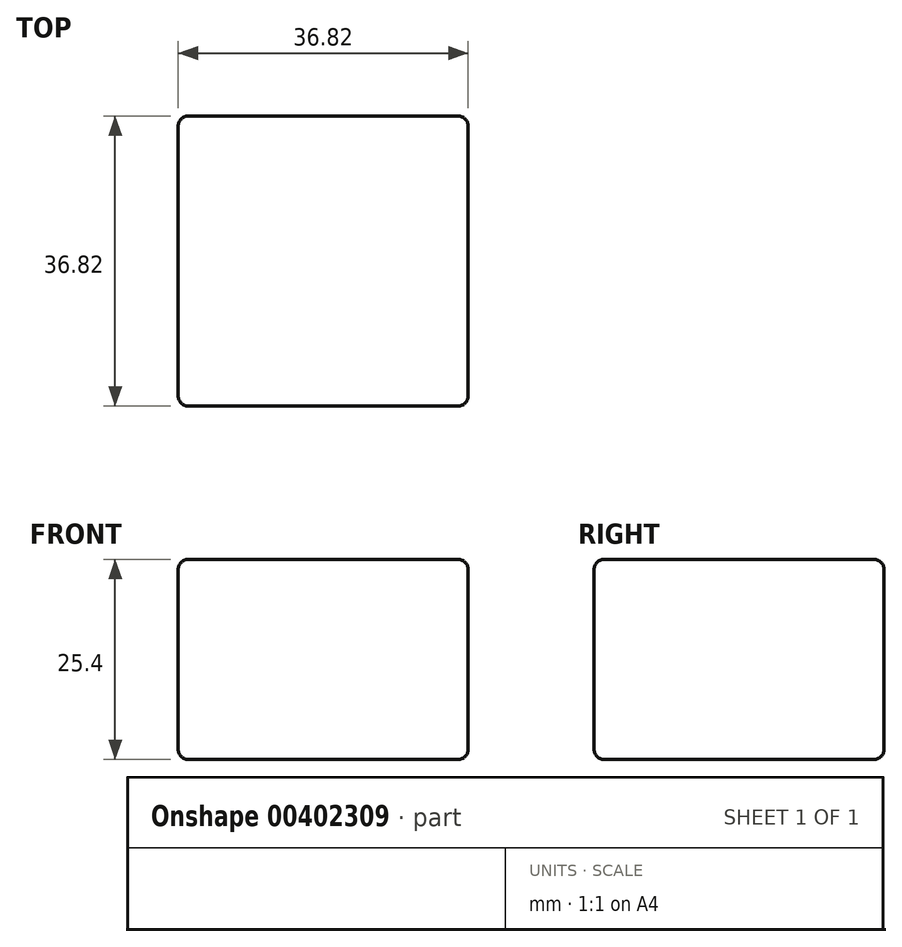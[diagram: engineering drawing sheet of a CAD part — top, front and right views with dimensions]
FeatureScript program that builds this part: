
annotation { "Feature Type Name" : "Feature", "Feature Type Description" : "" }
export const myFeature = defineFeature(function(context is Context, id is Id, definition is map)
    precondition{}
    {
        {
            var Q0;
            Q0=qCreatedBy(makeId("Top.planeOp"),FACE);
            var sketch = newSketch(context, id + "F0", { "sketchPlane" : qUnion([Q0])});
            skLineSegment(sketch, "E0.bottom", {"start": v(-18.41, 18.41) * mm, "end": v(18.42, 18.41) * mm});
            skLineSegment(sketch, "E0.top", {"start": v(-18.42, -18.41) * mm, "end": v(18.41, -18.41) * mm});
            skLineSegment(sketch, "E0.left", {"start": v(-18.41, 18.41) * mm, "end": v(-18.42, -18.41) * mm});
            skLineSegment(sketch, "E0.right", {"start": v(18.42, 18.41) * mm, "end": v(18.41, -18.41) * mm});
            skPoint(sketch, "E0.middle", {"position": v(0, 0) * mm});
            skSolve(sketch);
        }
        {
            var Q0;
            Q0 = qSketchRegion(id + "F0", true);
            extrude(context, id + "F1", {"entities" : qUnion([Q0]), "depth" : 25.4 * mm, "symmetric" : true});
        }
        {
            var Q0;
            Q0=makeQuery(id+"F1.opExtrude","CAP_EDGE",EDGE,{"disambiguationData":[OSD([sQuery(id+"F0.wireOp",EDGE,"E0.top")])],"isStart":false});
            var Q1;
            Q1=makeQuery(id+"F1.opExtrude","CAP_EDGE",EDGE,{"disambiguationData":[OSD([sQuery(id+"F0.wireOp",EDGE,"E0.right")])],"isStart":false});
            var Q2;
            Q2=makeQuery(id+"F1.opExtrude","SWEPT_EDGE",EDGE,{"disambiguationData":[OSD([sQuery(id+"F0.wireOp",EDGE,"E0.top"),sQuery(id+"F0.wireOp",EDGE,"E0.right")])]});
            var Q3;
            Q3=makeQuery(id+"F1.opExtrude","CAP_EDGE",EDGE,{"disambiguationData":[OSD([sQuery(id+"F0.wireOp",EDGE,"E0.right")])],"isStart":true});
            var Q4;
            Q4=makeQuery(id+"F1.opExtrude","CAP_EDGE",EDGE,{"disambiguationData":[OSD([sQuery(id+"F0.wireOp",EDGE,"E0.top")])],"isStart":true});
            var Q5;
            Q5=makeQuery(id+"F1.opExtrude","SWEPT_FACE",FACE,{"disambiguationData":[OSD([sQuery(id+"F0.wireOp",EDGE,"E0.left")])]});
            var Q6;
            Q6=makeQuery(id+"F1.opExtrude","SWEPT_FACE",FACE,{"disambiguationData":[OSD([sQuery(id+"F0.wireOp",EDGE,"E0.bottom")])]});
            fillet(context, id + "F2", {"entities" : qUnion([Q0, Q1, Q2, Q3, Q4, Q5, Q6]), "radius" : 1.27 * mm, "tangentPropagation" : true, "allowEdgeOverflow" : false});
        }
    });
